# Revit family: P200921MX-025c_MEW9630FZ
name_source: partatom
category: Specialty Equipment
units: mm (PartAtom-declared; Revit-internal decimal feet)

## family parameters
Always vertical = Yes
Cut with Voids When Loaded = No
Enable Cutting in Views = No
Maintain Annotation Orientation = No
Part Type = Normal
Room Calculation Point = No
Round Connector Dimension = Use Diameter
Shared = No
Work Plane-Based = No

## types (1)
- MEW9630FZ
    Accent Material = ARCAT - Plastic - White
    Amps = 0 A
    Body Material = ARCAT - Metal - Steel - Stainless
    Clearance Material = ARCAT - Clearance
    Default Elevation = 0"
    Depth = 26 7/8"
    Description = 30-Inch Wide Double Wall Oven With True Convection - 10.0 Cu. Ft.
FOUR MURAL DOUBLE À CONVECTION VÉRITABLE, 30 PO, 10 PI3
    Dimension Guide = http://access.whirlpool.com Guide&sku=MEW9630FZ&language=EN
http://access.whirlpool.com Guide&sku=MEW9630FZ&language=EN
    Display Panel Material = ARCAT - Glass - Tempered - Black
    Door Material = ARCAT - Metal - Steel - Stainless
    Energy Guide = http://access.whirlpool.com Guide&sku=MEW9630FZ&language=FR
http://access.whirlpool.com Guide&sku=MEW9630FZ&language=FR
    Family Name = Cooking
    Feature 1 = Power Preheat
Préchauffage rapide
    Feature 2 = True Convection With Fan & Third Element
Convection véritable avec troisième élément
    Feature 3 = FIT System
Système d'installation FIT
    Glass Material = ARCAT - Glass - Tempered - Black
    Handle Material = ARCAT - Metal - Steel - Gray
    Height = 51 3/16"
    Installation-Fabrication = http://access.whirlpool.com Instruction&sku=MEW9630FZ&language=EN
http://access.whirlpool.com Instruction&sku=MEW9630FZ&language=FR
    Manufacturer = Maytag
    Model = MEW9630FZ
    Voltage = 0 V
    Width = 30"

## geometry (parser evidence)
native form markers: Sweep x6
no freeform markers — native parametric forms only
